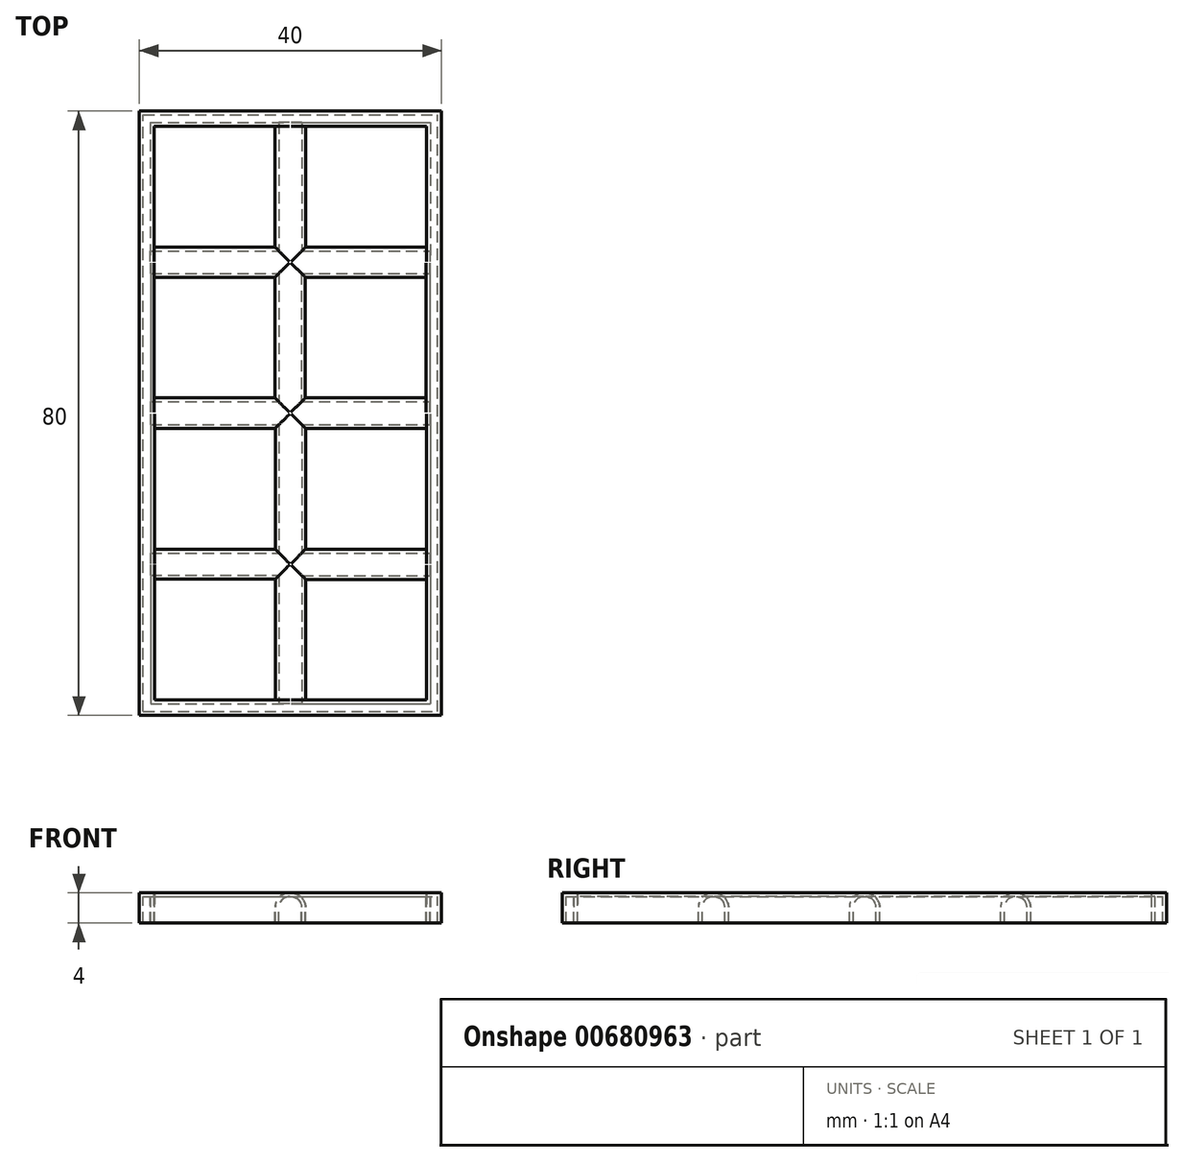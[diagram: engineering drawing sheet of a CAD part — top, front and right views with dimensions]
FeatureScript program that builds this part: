
annotation { "Feature Type Name" : "Feature", "Feature Type Description" : "" }
export const myFeature = defineFeature(function(context is Context, id is Id, definition is map)
    precondition{}
    {
        {
            var Q0;
            Q0=qCreatedBy(makeId("Top.planeOp"),FACE);
            var sketch = newSketch(context, id + "F0", { "sketchPlane" : qUnion([Q0])});
            skLineSegment(sketch, "E0.bottom", {"start": v(0, 0) * mm, "end": v(40, 0) * mm});
            skLineSegment(sketch, "E0.top", {"start": v(0, 80) * mm, "end": v(40, 80) * mm});
            skLineSegment(sketch, "E0.left", {"start": v(0, 0) * mm, "end": v(0, 80) * mm});
            skLineSegment(sketch, "E0.right", {"start": v(40, 0) * mm, "end": v(40, 80) * mm});
            skPoint(sketch, "E1", {"position": v(20, 80) * mm});
            skPoint(sketch, "E2", {"position": v(0, 60) * mm});
            skPoint(sketch, "E3", {"position": v(0, 40) * mm});
            skPoint(sketch, "E4", {"position": v(0, 20) * mm});
            skPoint(sketch, "E5", {"position": v(2, 80) * mm});
            skPoint(sketch, "E6", {"position": v(38, 80) * mm});
            skPoint(sketch, "E7", {"position": v(0, 78) * mm});
            skPoint(sketch, "E8", {"position": v(0, 62) * mm});
            skPoint(sketch, "E9", {"position": v(22, 80) * mm});
            skPoint(sketch, "E10", {"position": v(18, 80) * mm});
            skPoint(sketch, "E11", {"position": v(0, 58) * mm});
            skPoint(sketch, "E12", {"position": v(0, 42) * mm});
            skPoint(sketch, "E13", {"position": v(0, 38) * mm});
            skPoint(sketch, "E14", {"position": v(0, 22) * mm});
            skPoint(sketch, "E15", {"position": v(0, 18) * mm});
            skPoint(sketch, "E16", {"position": v(0, 2) * mm});
            skLineSegment(sketch, "E17.bottom", {"start": v(1.97, 78) * mm, "end": v(17.97, 78) * mm});
            skLineSegment(sketch, "E17.top", {"start": v(1.97, 62) * mm, "end": v(17.97, 62) * mm});
            skLineSegment(sketch, "E17.left", {"start": v(1.97, 78) * mm, "end": v(1.97, 62) * mm});
            skLineSegment(sketch, "E17.right", {"start": v(17.97, 78) * mm, "end": v(17.97, 62) * mm});
            skLineSegment(sketch, "E18.bottom", {"start": v(22.01, 78) * mm, "end": v(38.01, 78) * mm});
            skLineSegment(sketch, "E18.top", {"start": v(22.01, 62) * mm, "end": v(38.01, 62) * mm});
            skLineSegment(sketch, "E18.left", {"start": v(22.01, 78) * mm, "end": v(22.01, 62) * mm});
            skLineSegment(sketch, "E18.right", {"start": v(38.01, 78) * mm, "end": v(38.01, 62) * mm});
            skLineSegment(sketch, "E19.bottom", {"start": v(1.97, 58.02) * mm, "end": v(17.97, 58.02) * mm});
            skLineSegment(sketch, "E19.top", {"start": v(1.97, 42.02) * mm, "end": v(17.97, 42.02) * mm});
            skLineSegment(sketch, "E19.left", {"start": v(1.97, 58.02) * mm, "end": v(1.97, 42.02) * mm});
            skLineSegment(sketch, "E19.right", {"start": v(17.97, 58.02) * mm, "end": v(17.97, 42.02) * mm});
            skLineSegment(sketch, "E20.bottom", {"start": v(21.96, 58.02) * mm, "end": v(37.96, 58.02) * mm});
            skLineSegment(sketch, "E20.top", {"start": v(21.96, 42.02) * mm, "end": v(37.96, 42.02) * mm});
            skLineSegment(sketch, "E20.left", {"start": v(21.96, 58.02) * mm, "end": v(21.96, 42.02) * mm});
            skLineSegment(sketch, "E20.right", {"start": v(37.96, 58.02) * mm, "end": v(37.96, 42.02) * mm});
            skLineSegment(sketch, "E21.bottom", {"start": v(2, 38) * mm, "end": v(18, 38) * mm});
            skLineSegment(sketch, "E21.top", {"start": v(2, 22) * mm, "end": v(18, 22) * mm});
            skLineSegment(sketch, "E21.left", {"start": v(2, 38) * mm, "end": v(2, 22) * mm});
            skLineSegment(sketch, "E21.right", {"start": v(18, 38) * mm, "end": v(18, 22) * mm});
            skLineSegment(sketch, "E22.bottom", {"start": v(22, 38) * mm, "end": v(38, 38) * mm});
            skLineSegment(sketch, "E22.top", {"start": v(22, 22) * mm, "end": v(38, 22) * mm});
            skLineSegment(sketch, "E22.left", {"start": v(22, 38) * mm, "end": v(22, 22) * mm});
            skLineSegment(sketch, "E22.right", {"start": v(38, 38) * mm, "end": v(38, 22) * mm});
            skLineSegment(sketch, "E23.bottom", {"start": v(2, 18.03) * mm, "end": v(18, 18.03) * mm});
            skLineSegment(sketch, "E23.top", {"start": v(2, 2.03) * mm, "end": v(18, 2.03) * mm});
            skLineSegment(sketch, "E23.left", {"start": v(2, 18.03) * mm, "end": v(2, 2.03) * mm});
            skLineSegment(sketch, "E23.right", {"start": v(18, 18.03) * mm, "end": v(18, 2.03) * mm});
            skLineSegment(sketch, "E24.bottom", {"start": v(22.02, 18.01) * mm, "end": v(38, 18.01) * mm});
            skLineSegment(sketch, "E24.top", {"start": v(22.02, 2.03) * mm, "end": v(38, 2.03) * mm});
            skLineSegment(sketch, "E24.left", {"start": v(22.02, 18.01) * mm, "end": v(22.02, 2.03) * mm});
            skLineSegment(sketch, "E24.right", {"start": v(38, 18.01) * mm, "end": v(38, 2.03) * mm});
            skSolve(sketch);
        }
        {
            var Q0;
            Q0=makeQuery(id+"F0.imprint","IMPRINT",FACE,{"disambiguationData":[TD([[makeQuery(id+"F0.imprint","IMPRINT",EDGE,{"derivedFrom":sQuery(id+"F0.wireOp",EDGE,"E0.bottom")}),1.0]])]});
            extrude(context, id + "F1", {"entities" : qUnion([Q0]), "oppositeDirection" : true, "depth" : 4 * mm, "offsetDistance" : 25 * mm});
        }
        {
            var Q0;
            Q0=makeQuery(id+"F1.opExtrude","CAP_EDGE",EDGE,{"disambiguationData":[OSD([sQuery(id+"F0.wireOp",EDGE,"E21.right")])],"isStart":true});
            var Q1;
            Q1=makeQuery(id+"F1.opExtrude","CAP_EDGE",EDGE,{"disambiguationData":[OSD([sQuery(id+"F0.wireOp",EDGE,"E22.left")])],"isStart":true});
            var Q2;
            Q2=makeQuery(id+"F1.opExtrude","CAP_EDGE",EDGE,{"disambiguationData":[OSD([sQuery(id+"F0.wireOp",EDGE,"E22.bottom")])],"isStart":true});
            var Q3;
            Q3=makeQuery(id+"F1.opExtrude","CAP_EDGE",EDGE,{"disambiguationData":[OSD([sQuery(id+"F0.wireOp",EDGE,"E21.bottom")])],"isStart":true});
            var Q4;
            Q4=makeQuery(id+"F1.opExtrude","CAP_EDGE",EDGE,{"disambiguationData":[OSD([sQuery(id+"F0.wireOp",EDGE,"E23.bottom")])],"isStart":true});
            var Q5;
            Q5=makeQuery(id+"F1.opExtrude","CAP_EDGE",EDGE,{"disambiguationData":[OSD([sQuery(id+"F0.wireOp",EDGE,"E23.right")])],"isStart":true});
            var Q6;
            Q6=makeQuery(id+"F1.opExtrude","CAP_EDGE",EDGE,{"disambiguationData":[OSD([sQuery(id+"F0.wireOp",EDGE,"E17.right")])],"isStart":true});
            var Q7;
            Q7=makeQuery(id+"F1.opExtrude","CAP_EDGE",EDGE,{"disambiguationData":[OSD([sQuery(id+"F0.wireOp",EDGE,"E18.left")])],"isStart":true});
            var Q8;
            Q8=makeQuery(id+"F1.opExtrude","CAP_EDGE",EDGE,{"disambiguationData":[OSD([sQuery(id+"F0.wireOp",EDGE,"E17.top")])],"isStart":true});
            var Q9;
            Q9=makeQuery(id+"F1.opExtrude","CAP_EDGE",EDGE,{"disambiguationData":[OSD([sQuery(id+"F0.wireOp",EDGE,"E19.bottom")])],"isStart":true});
            var Q10;
            Q10=makeQuery(id+"F1.opExtrude","CAP_EDGE",EDGE,{"disambiguationData":[OSD([sQuery(id+"F0.wireOp",EDGE,"E18.top")])],"isStart":true});
            var Q11;
            Q11=makeQuery(id+"F1.opExtrude","CAP_EDGE",EDGE,{"disambiguationData":[OSD([sQuery(id+"F0.wireOp",EDGE,"E20.top")])],"isStart":true});
            var Q12;
            Q12=makeQuery(id+"F1.opExtrude","CAP_EDGE",EDGE,{"disambiguationData":[OSD([sQuery(id+"F0.wireOp",EDGE,"E19.right")])],"isStart":true});
            var Q13;
            Q13=makeQuery(id+"F1.opExtrude","CAP_EDGE",EDGE,{"disambiguationData":[OSD([sQuery(id+"F0.wireOp",EDGE,"E19.top")])],"isStart":true});
            var Q14;
            Q14=makeQuery(id+"F1.opExtrude","CAP_EDGE",EDGE,{"disambiguationData":[OSD([sQuery(id+"F0.wireOp",EDGE,"E21.top")])],"isStart":true});
            var Q15;
            Q15=makeQuery(id+"F1.opExtrude","CAP_EDGE",EDGE,{"disambiguationData":[OSD([sQuery(id+"F0.wireOp",EDGE,"E22.top")])],"isStart":true});
            var Q16;
            Q16=makeQuery(id+"F1.opExtrude","CAP_EDGE",EDGE,{"disambiguationData":[OSD([sQuery(id+"F0.wireOp",EDGE,"E24.bottom")])],"isStart":true});
            var Q17;
            Q17=makeQuery(id+"F1.opExtrude","CAP_EDGE",EDGE,{"disambiguationData":[OSD([sQuery(id+"F0.wireOp",EDGE,"E24.left")])],"isStart":true});
            var Q18;
            Q18=makeQuery(id+"F1.opExtrude","CAP_EDGE",EDGE,{"disambiguationData":[OSD([sQuery(id+"F0.wireOp",EDGE,"E20.left")])],"isStart":true});
            var Q19;
            Q19=makeQuery(id+"F1.opExtrude","CAP_EDGE",EDGE,{"disambiguationData":[OSD([sQuery(id+"F0.wireOp",EDGE,"E20.bottom")])],"isStart":true});
            fillet(context, id + "F2", {"entities" : qUnion([Q0, Q1, Q2, Q3, Q4, Q5, Q6, Q7, Q8, Q9, Q10, Q11, Q12, Q13, Q14, Q15, Q16, Q17, Q18, Q19]), "radius" : 1.9 * mm, "tangentPropagation" : true, "allowEdgeOverflow" : false});
        }
        {
            var Q0;
            Q0=makeQuery(id+"F1.opExtrude","CAP_FACE",FACE,{"disambiguationData":[OSD([sQuery(id+"F0.wireOp",EDGE,"E0.bottom"),sQuery(id+"F0.wireOp",EDGE,"E0.top"),sQuery(id+"F0.wireOp",EDGE,"E0.left"),sQuery(id+"F0.wireOp",EDGE,"E0.right"),sQuery(id+"F0.wireOp",EDGE,"E17.bottom"),sQuery(id+"F0.wireOp",EDGE,"E17.top"),sQuery(id+"F0.wireOp",EDGE,"E17.left"),sQuery(id+"F0.wireOp",EDGE,"E17.right"),sQuery(id+"F0.wireOp",EDGE,"E18.bottom"),sQuery(id+"F0.wireOp",EDGE,"E18.top"),sQuery(id+"F0.wireOp",EDGE,"E18.left"),sQuery(id+"F0.wireOp",EDGE,"E18.right"),sQuery(id+"F0.wireOp",EDGE,"E19.bottom"),sQuery(id+"F0.wireOp",EDGE,"E19.top"),sQuery(id+"F0.wireOp",EDGE,"E19.left"),sQuery(id+"F0.wireOp",EDGE,"E19.right"),sQuery(id+"F0.wireOp",EDGE,"E20.bottom"),sQuery(id+"F0.wireOp",EDGE,"E20.top"),sQuery(id+"F0.wireOp",EDGE,"E20.left"),sQuery(id+"F0.wireOp",EDGE,"E20.right"),sQuery(id+"F0.wireOp",EDGE,"E21.bottom"),sQuery(id+"F0.wireOp",EDGE,"E21.top"),sQuery(id+"F0.wireOp",EDGE,"E21.left"),sQuery(id+"F0.wireOp",EDGE,"E21.right"),sQuery(id+"F0.wireOp",EDGE,"E22.bottom"),sQuery(id+"F0.wireOp",EDGE,"E22.top"),sQuery(id+"F0.wireOp",EDGE,"E22.left"),sQuery(id+"F0.wireOp",EDGE,"E22.right"),sQuery(id+"F0.wireOp",EDGE,"E23.bottom"),sQuery(id+"F0.wireOp",EDGE,"E23.top"),sQuery(id+"F0.wireOp",EDGE,"E23.left"),sQuery(id+"F0.wireOp",EDGE,"E23.right"),sQuery(id+"F0.wireOp",EDGE,"E24.bottom"),sQuery(id+"F0.wireOp",EDGE,"E24.top"),sQuery(id+"F0.wireOp",EDGE,"E24.left"),sQuery(id+"F0.wireOp",EDGE,"E24.right")])],"isStart":false});
            shell(context, id + "F3", {"entities" : qUnion([Q0]), "thickness" : 0.5 * mm});
        }
    });
